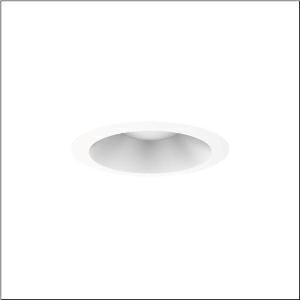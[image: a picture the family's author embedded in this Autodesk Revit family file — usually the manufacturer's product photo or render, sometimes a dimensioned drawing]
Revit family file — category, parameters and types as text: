
# Revit family: lunis_31_midi_51dn157g32
name_source: partatom
category: Lighting Fixtures
units: mm (PartAtom-declared; Revit-internal decimal feet)

## family parameters
Cut with Voids When Loaded = No
Host = Face
Light Source = No
Part Type = Normal
Room Calculation Point = No
Round Connector Dimension = Use Diameter
Shared = No

## types (1)
- Lunis 31 midi (1 x LED, 2000 lm, 17 W, 3000K)
    Apparent Load = 17 VA
    CIE Flux Codes = 89 99 100 100 100
    Color Rendering = 80
    Color Temperature = 3000K
    Default Elevation = 1800 mm
    Description = Lunis 31,  midi, downlight, light control with lens, light emission: direct distribution, LED rated luminous flux: 2.000lm, light colour: 830, mains connection: 220..240V, AC, 50/60Hz, housing, white, protection rating (complete): IP20, protection rating (on room side): IP54, insulation class (complete): insulation class II (safety insulation), certification: CE, packaging unit: 1 piece
    Height = 0 mm  [stored 0 ft]
    Lamp = 1 x LED
    Lamp Light Flux = 2000 lm
    Lamp Power = 17 W
    Lamp count = 1
    Length = 259 mm
    Luminous efficacy = 118 lm/W
    Manufacturer = Siteco
    ModVariant = No
    Model = 51DN157G32
    Mounting Place = Ceiling
    Mounting Type = Recessed
    Number of Poles = 1
    OnlyDefault = Yes
    Power Factor = 1
    Product Name = Lunis 31 midi
    Product group = downlight
    ProductGroupID = 400
    Protection Class = Protection class II
    Protection Degree = IP 20
    RLX_Detail_Level = 1
    RLX_Emergency_Light_Flux = 0 lm
    RLX_Emergency_Type = 0
    RLX_Emergency_Type_DB = No
    RlxData = <blob elided: 23729 chars, md5=471187b1>
    Socket = socket
    Standby Power = 0 W
    System Light Flux = 2000 lm
    System Power = 17 W
    Type Comments = Product without accessories
    Type Image = l_1006711.jpg
    URL = http://relux.com
    VarID = ---
    Voltage = 0 V
    Weight = 0.00 kg
    Width = 0 mm  [stored 0 ft]

note: [stored X ft] marks values corroborated as IEEE doubles in the binary element streams (Revit-internal decimal feet)

## geometry (parser evidence)
native form markers: Blend x4, Sweep x10
no freeform markers — native parametric forms only
